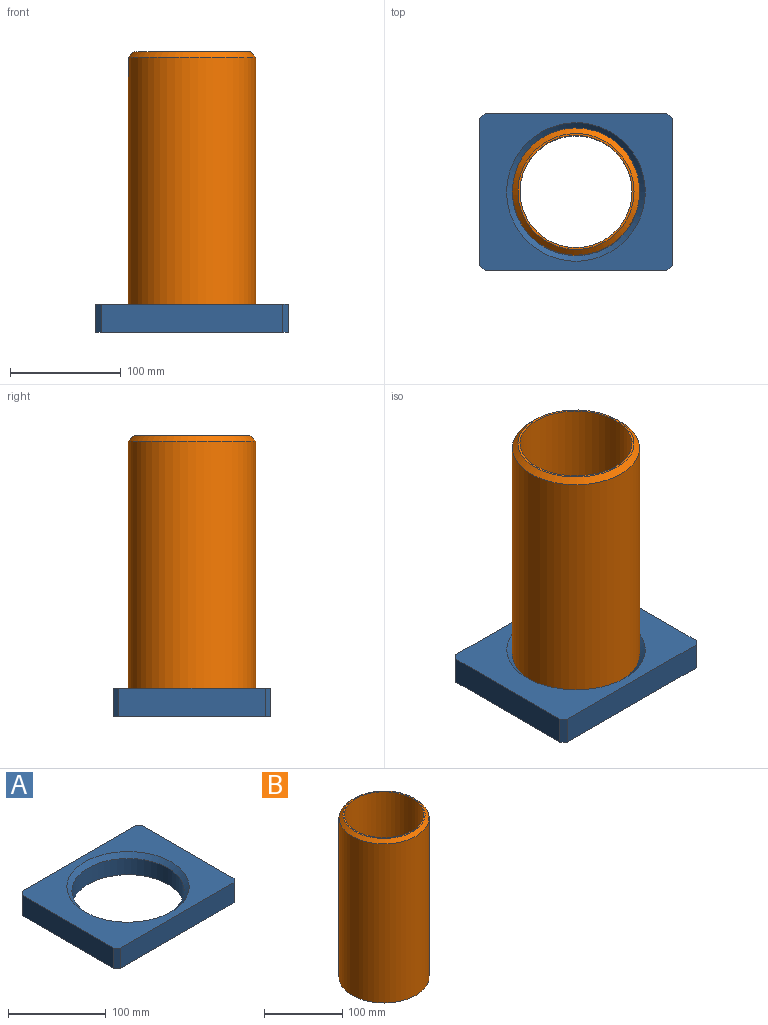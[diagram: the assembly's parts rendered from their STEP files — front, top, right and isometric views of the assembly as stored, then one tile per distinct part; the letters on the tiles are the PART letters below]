
ASSEMBLY  parts=2 mates=1
PART A: 12 faces, bbox 174.5x142.9x25.4 mm
  f0: plane 164.31x25.4mm, normal (0,1,0), area 4173.6mm2, adj f5,f6,f7,f10
  f1: plane 132.72x25.4mm, normal (-1,0,0), area 3371.1mm2, adj f5,f6,f9,f10
  f2: plane 164.31x25.4mm, normal (0,-1,0), area 4173.6mm2, adj f5,f6,f8,f9
  f3: cylinder r=57.59mm len=115.19mm, axis (0,0,-1), area 7353.1mm2, adj f6,f11
  f4: plane 132.72x25.4mm, normal (1,0,0), area 3371.1mm2, adj f5,f6,f7,f8
  f5: plane 174.47x142.88mm, normal (0,0,1), area 12537.8mm2, adj f0,f1,f2,f4,f7,f8,f9,f10
  f6: plane 174.47x142.88mm, normal (0,0,-1), area 14457.2mm2, adj f0,f1,f2,f3,f4,f7,f8,f9
  f7: plane 25.4x5.08mm, normal (0.71,0.71,0), area 182.5mm2, adj f0,f4,f5,f6
  f8: plane 25.4x5.08mm, normal (0.71,-0.71,0), area 182.5mm2, adj f2,f4,f5,f6
  f9: plane 25.4x5.08mm, normal (-0.71,-0.71,0), area 182.5mm2, adj f1,f2,f5,f6
  f10: plane 25.4x5.08mm, normal (-0.71,0.71,0), area 182.5mm2, adj f0,f1,f5,f6
  f11: cone r=57.59mm half-angle=45deg, axis (0,0,1), area 2714.4mm2, adj f3,f5
PART B: 5 faces, bbox 115.1x115.1x254 mm
  f0: cylinder r=50.72mm len=254mm, axis (0,0,1), area 80947.5mm2, adj f2,f3
  f1: cylinder r=57.57mm len=248.92mm, axis (0,0,1), area 90033.9mm2, adj f3,f4
  f2: plane 104.97x104.97mm, normal (0,0,1), area 572.2mm2, adj f0,f4
  f3: plane 115.13x115.13mm, normal (0,0,-1), area 2328.6mm2, adj f0,f1
  f4: cone r=52.49mm half-angle=45deg, axis (0,0,-1), area 2483.9mm2, adj f1,f2
PLACE A t=(-54.37,-48.58,-151.66)mm
PLACE B t=(-54.37,-48.58,-151.66)mm
MATE fastened B.f1 <-> A.f3  axis (0,0,-1) through (-54.37,-48.58,-151.66)mm
